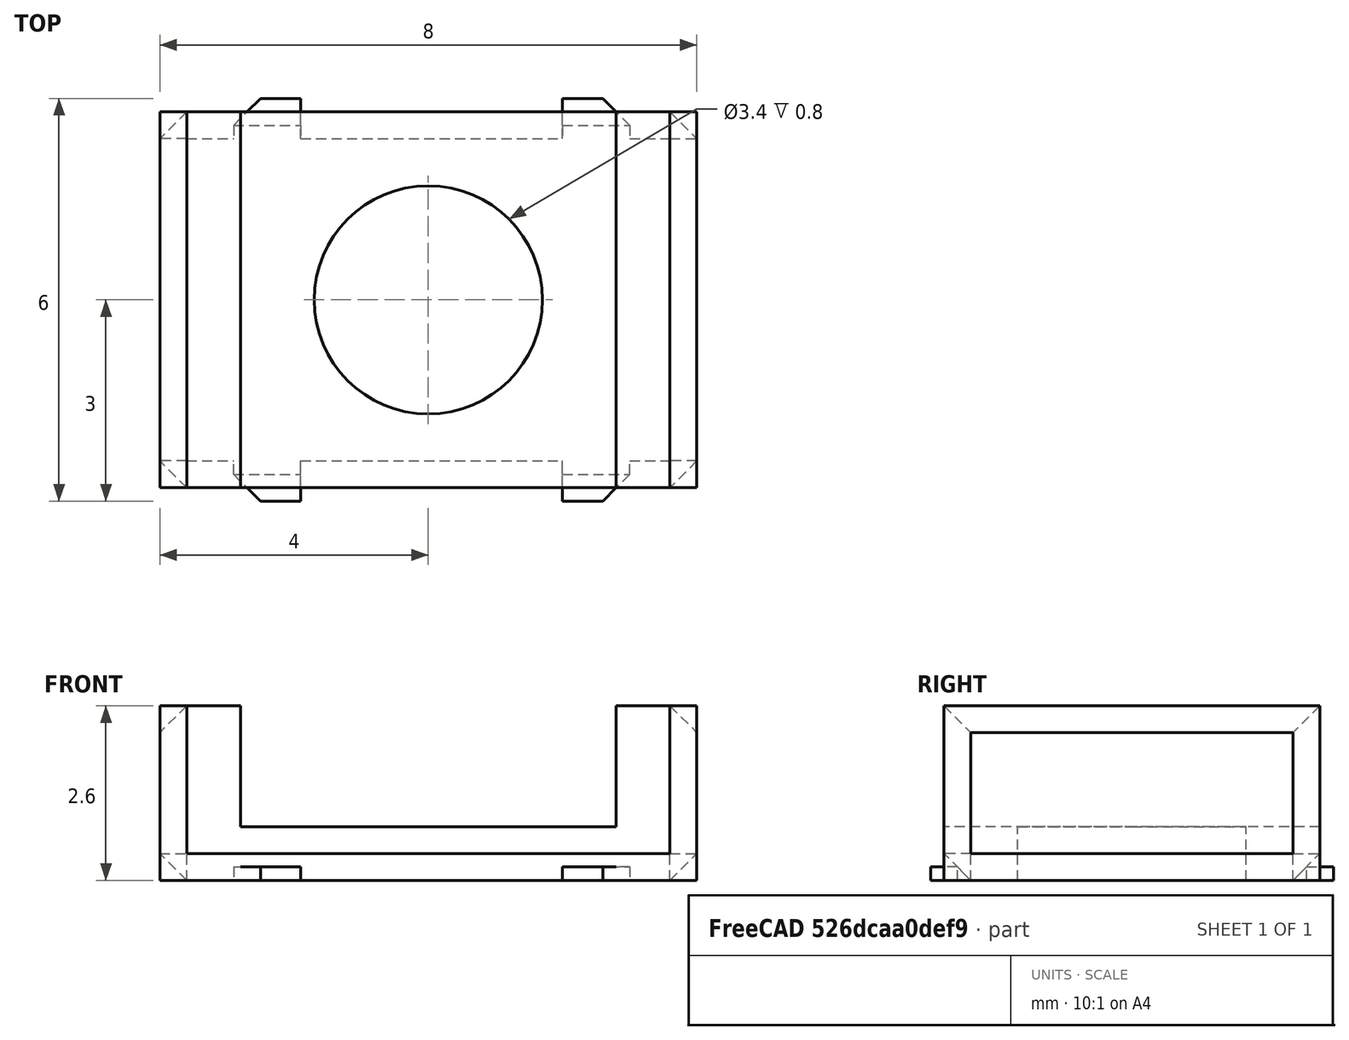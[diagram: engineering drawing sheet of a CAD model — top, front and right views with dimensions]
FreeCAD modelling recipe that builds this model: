
FCSTD DOCUMENT  (FreeCAD 0.18R16146 (Git))
Label: nut-holder
License: All rights reserved
LicenseURL: http://en.wikipedia.org/wiki/All_rights_reserved
objects: Part::Box×5, Part::MultiFuse×3, Part::Chamfer×2, Part::Cylinder×1, Part::Feature×1, Part::Cut×1
note: 13 computed .brp shape members not serialized (recipe doc carries the construction recipe); baked Part::Feature solids carry a one-line shape summary decoded from their .brp

FEATURE [Part::Box] Box  label="Cube"
  AttacherType = Attacher::AttachEngine3D
  Height = 2.6
  Length = 1.2
  Placement = pos=(-4,-2.8,0) rot=(0,0,1;0rad)
  Width = 5.6
FEATURE [Part::Box] Box002  label="Cube002"
  AttacherType = Attacher::AttachEngine3D
  Height = 2.6
  Length = 1.2
  Placement = pos=(2.8,-2.8,0) rot=(0,0,1;0rad)
  Width = 5.6
FEATURE [Part::Cylinder] Cylinder
  Angle = 360
  AttacherType = Attacher::AttachEngine3D
  Height = 10
  Radius = 1.7
FEATURE [Part::Box] Box001  label="Cube001"
  AttacherType = Attacher::AttachEngine3D
  Height = 0.8
  Length = 8
  Placement = pos=(-4,-2.8,0) rot=(0,0,1;0rad)
  Width = 5.6
FEATURE [Part::MultiFuse] Fusion
  Shapes = -> [Box,Box001,Box002]
FEATURE [Part::Feature] Fusion003
  shape: bbox 8 x 5.6 x 2.6 mm, 10 faces (baked)
FEATURE [Part::Cut] Cut
  Base = -> Fusion003
  Tool = -> Cylinder
FEATURE [Part::Chamfer] Chamfer
  Base = -> Cut
  Edges = 10 edges r=0.4: [Edge1,Edge5,Edge6,Edge7,Edge12,Edge13,Edge16,Edge17,Edge21,Edge26]
FEATURE [Part::Box] Box003  label="Cube003"
  AttacherType = Attacher::AttachEngine3D
  Height = 0.2
  Length = 1
  Placement = pos=(2,-3,0) rot=(0,0,1;0rad)
  Width = 6
FEATURE [Part::Box] Box004  label="Cube004"
  AttacherType = Attacher::AttachEngine3D
  Height = 0.2
  Length = 1
  Placement = pos=(-2.9,-3,0) rot=(0,0,1;0rad)
  Width = 6
FEATURE [Part::MultiFuse] Fusion004
  Shapes = -> [Box004,Box003]
FEATURE [Part::Chamfer] Chamfer001
  Base = -> Fusion004
  Edges = 4 edges r=0.4: [Edge1,Edge3,Edge17,Edge19]
FEATURE [Part::MultiFuse] Fusion005
  Shapes = -> [Chamfer,Chamfer001]
